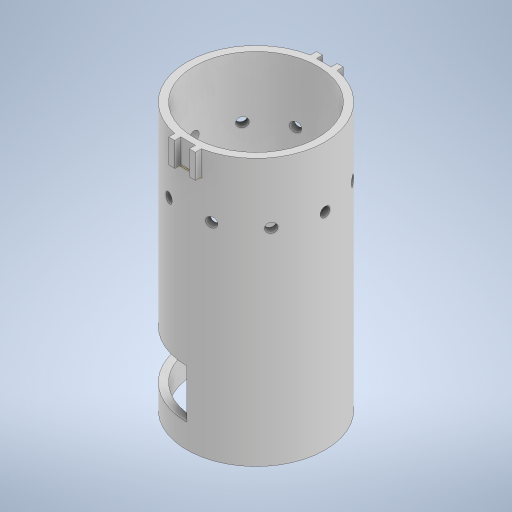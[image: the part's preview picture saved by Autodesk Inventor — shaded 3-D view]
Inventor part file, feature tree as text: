
AUTODESK INVENTOR PART (.ipt)
format: ipt  version: 2024.3 (Build 283343000, 343)  size: 338,944 bytes
history: native  units: mm
features: sketch x7, extrude x6, plane x2, mirror x2, pattern_circular x1
ambient origin geometry x8: Origin, YZ Plane, XZ Plane, XY Plane, X Axis, Y Axis, Z Axis, Center Point
bodies: Solid1 (feature_tree)
feature tree (18):
  extrude  "Extrusion1"  Depth=102.0mm
  extrude  "Extrusion2"  Depth=20.0mm TaperAngle=0.0deg
  plane  "Work Plane1"
  extrude  "Extrusion3"  Depth=5.0mm
  mirror  "Mirror1"
  mirror  "Mirror2"
  sketch  "Sketch4"  dims[d8=5.0mm d9=20.0mm d10=0.0mm]
  extrude  "Extrusion4"  Depth=20.0mm TaperAngle=0.0deg
  sketch  "Sketch5"  dims[d11=40.0mm d12=36.0mm]
  plane  "Work Plane2"
  extrude  "Extrusion6"  Depth=36.0mm
  extrude  "Extrusion7"  Depth=20.0mm
  pattern_circular  "Circular Pattern1"  [2 undecoded]
  sketch  "Sketch1"  dims[d0=114.0mm d1=102.0mm]
  sketch  "Sketch2"  dims[d2=220.0mm d3=0.0mm d4=20.0mm d5=0.0mm]
  sketch  "Sketch3"  dims[d6=0.0mm d7=5.0mm]
  sketch  "Sketch6"  dims[d13=2.0mm d14=20.0mm]
  sketch  "Sketch7"  dims[d15=0.0mm d16=0.0mm d19=21.99994mm d20=110.0mm d21=135.0deg d22=70.0mm d23=40.0mm d24=0.0mm d25=0.0mm d26=8.0mm d27=170.0mm d28=0.0mm d29=0.0mm d30=50.0mm d31=360.0deg]
note: 2 required parameter values undecoded (feature->parameter linkage not recoverable at this tier; creation-order binding heuristic only, values carry confidence <= 0.55)
